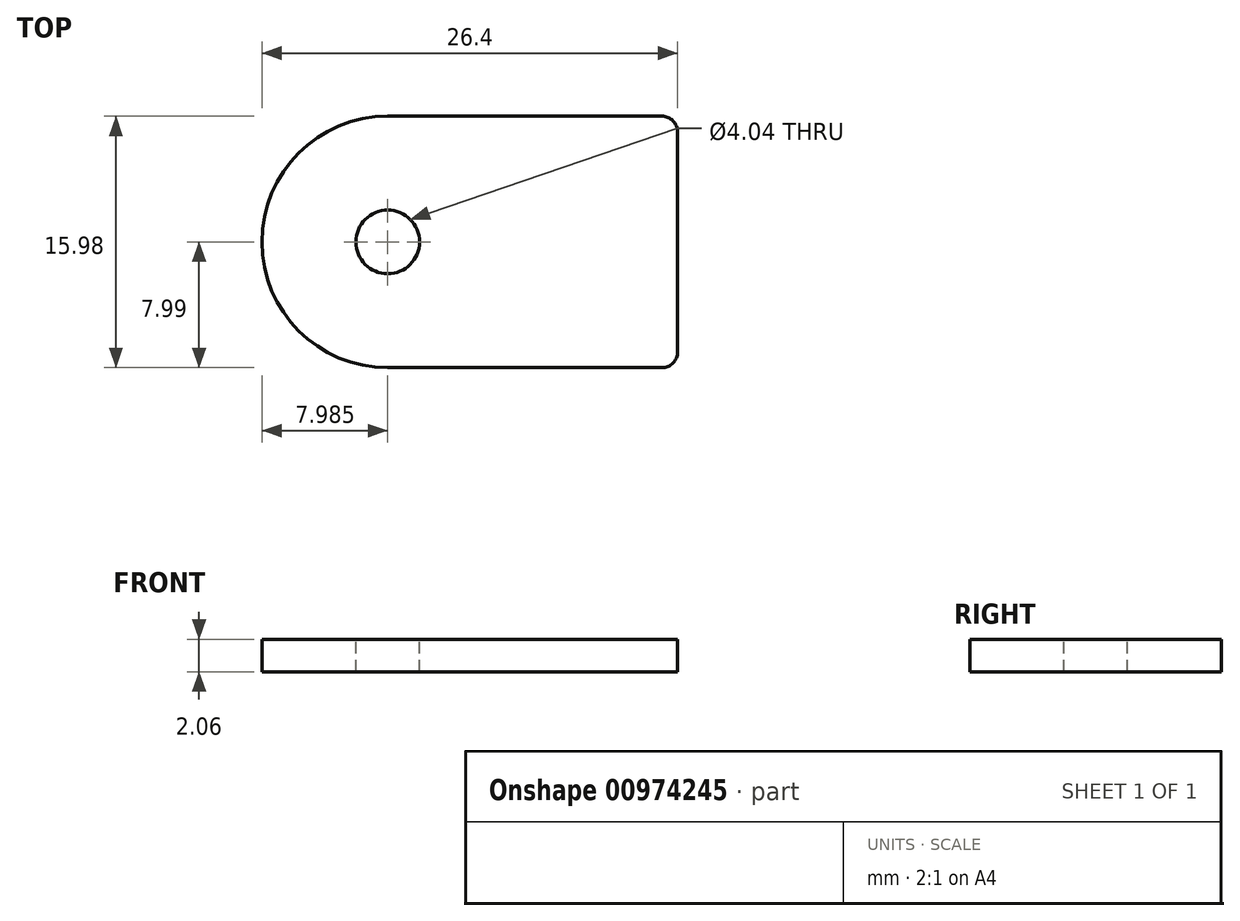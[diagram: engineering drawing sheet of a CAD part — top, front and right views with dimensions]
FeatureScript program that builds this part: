
annotation { "Feature Type Name" : "Feature", "Feature Type Description" : "" }
export const myFeature = defineFeature(function(context is Context, id is Id, definition is map)
    precondition{}
    {
        {
            var Q0;
            Q0=qCreatedBy(makeId("Top.planeOp"),FACE);
            var sketch = newSketch(context, id + "F0", { "sketchPlane" : qUnion([Q0])});
            skLineSegment(sketch, "E0.bottom", {"start": v(-1.02, 7.99) * mm, "end": v(-18.41, 7.99) * mm});
            skLineSegment(sketch, "E0.top", {"start": v(-1.02, -7.99) * mm, "end": v(-18.41, -7.99) * mm});
            skLineSegment(sketch, "E0.left", {"start": v(0, 6.97) * mm, "end": v(0, -6.97) * mm});
            skArc(sketch, "E1", {"start": v(-18.41, 7.99) * mm, "mid": v(-26.4, 0) * mm, "end": v(-18.41, -7.99) * mm});
            skCircle(sketch, "E2", {"center": v(-18.41, 0) * mm, "radius": 2.02 * mm});
            skPoint(sketch, "E3.visualSharp", {"position": v(0, 7.99) * mm});
            skArc(sketch, "E3.filletArc", {"start": v(0, 6.97) * mm, "mid": v(-0.3, 7.7) * mm, "end": v(-1.02, 7.99) * mm});
            skPoint(sketch, "E4.visualSharp", {"position": v(0, -7.99) * mm});
            skArc(sketch, "E4.filletArc", {"start": v(-1.02, -7.99) * mm, "mid": v(-0.3, -7.7) * mm, "end": v(0, -6.97) * mm});
            skSolve(sketch);
        }
        {
            var Q0;
            Q0 = qSketchRegion(id + "F0", true);
            extrude(context, id + "F1", {"entities" : qUnion([Q0]), "oppositeDirection" : true, "depth" : 2.06 * mm, "offsetDistance" : 25.4 * mm});
        }
    });
